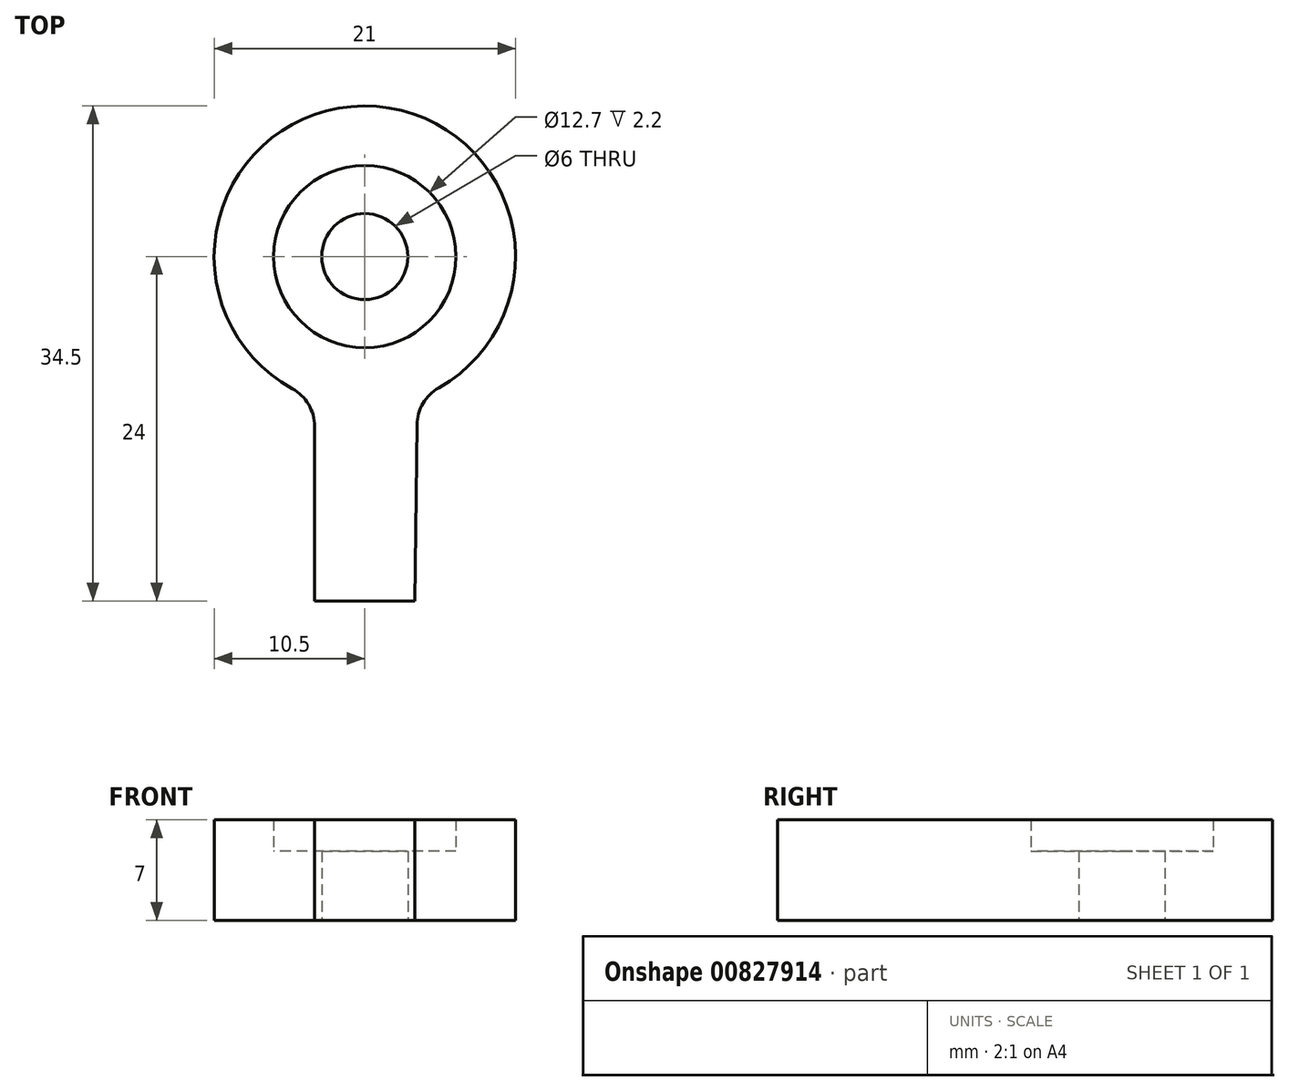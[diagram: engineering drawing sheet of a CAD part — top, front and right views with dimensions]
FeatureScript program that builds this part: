
annotation { "Feature Type Name" : "Feature", "Feature Type Description" : "" }
export const myFeature = defineFeature(function(context is Context, id is Id, definition is map)
    precondition{}
    {
        {
            var Q0;
            Q0=qCreatedBy(makeId("Top.planeOp"),FACE);
            var sketch = newSketch(context, id + "F0", { "sketchPlane" : qUnion([Q0])});
            skArc(sketch, "E0", {"start": v(3.66, -9.84) * mm, "mid": v(-0.08, 10.5) * mm, "end": v(-3.5, -9.9) * mm});
            skCircle(sketch, "E1", {"center": v(0, 0) * mm, "radius": 6.35 * mm});
            skLineSegment(sketch, "E2.top", {"start": v(-3.5, -24) * mm, "end": v(3.5, -24) * mm});
            skLineSegment(sketch, "E2.left", {"start": v(-3.5, -9.9) * mm, "end": v(-3.5, -24) * mm});
            skLineSegment(sketch, "E3", {"start": v(0, 0) * mm, "end": v(0, -24) * mm, "construction": true});
            skPoint(sketch, "E4.orphan", {"position": v(-3.5, 0) * mm});
            skLineSegment(sketch, "E5.trimOffspring", {"start": v(3.66, -9.84) * mm, "end": v(3.5, -24) * mm});
            skSolve(sketch);
        }
        {
            var Q0;
            Q0 = qSketchRegion(id + "F0", true);
            extrude(context, id + "F1", {"entities" : qUnion([Q0]), "depth" : 7 * mm, "offsetDistance" : 25 * mm});
        }
        {
            var Q0;
            Q0=makeQuery(id+"F1.opExtrude","SWEPT_EDGE",EDGE,{"disambiguationData":[OSD([sQuery(id+"F0.wireOp",EDGE,"E0"),sQuery(id+"F0.wireOp",EDGE,"E2.left")])]});
            var Q1;
            Q1=makeQuery(id+"F1.opExtrude","SWEPT_EDGE",EDGE,{"disambiguationData":[OSD([sQuery(id+"F0.wireOp",EDGE,"E0"),sQuery(id+"F0.wireOp",EDGE,"E5.trimOffspring")])]});
            fillet(context, id + "F2", {"entities" : qUnion([Q0, Q1]), "radius" : 3 * mm, "tangentPropagation" : true, "allowEdgeOverflow" : false});
        }
        {
            var Q0;
            Q0=makeQuery(id+"F1.opExtrude","CAP_FACE",FACE,{"disambiguationData":[OSD([sQuery(id+"F0.wireOp",EDGE,"E0"),sQuery(id+"F0.wireOp",EDGE,"E1"),sQuery(id+"F0.wireOp",EDGE,"E2.top"),sQuery(id+"F0.wireOp",EDGE,"E2.left"),sQuery(id+"F0.wireOp",EDGE,"E5.trimOffspring")])],"isStart":true});
            var sketch = newSketch(context, id + "F3", { "sketchPlane" : qUnion([Q0])});
            skCircle(sketch, "E6", {"center": v(0, 0) * mm, "radius": 3 * mm});
            skCircle(sketch, "E7.0", {"center": v(0, 0) * mm, "radius": 6.35 * mm});
            skSolve(sketch);
        }
        {
            var Q0;
            Q0 = qSketchRegion(id + "F3", true);
            extrude(context, id + "F4", {"entities" : qUnion([Q0]), "operationType" : NewBodyOperationType.ADD, "oppositeDirection" : true, "depth" : 4.8 * mm, "offsetDistance" : 25 * mm});
        }
    });
